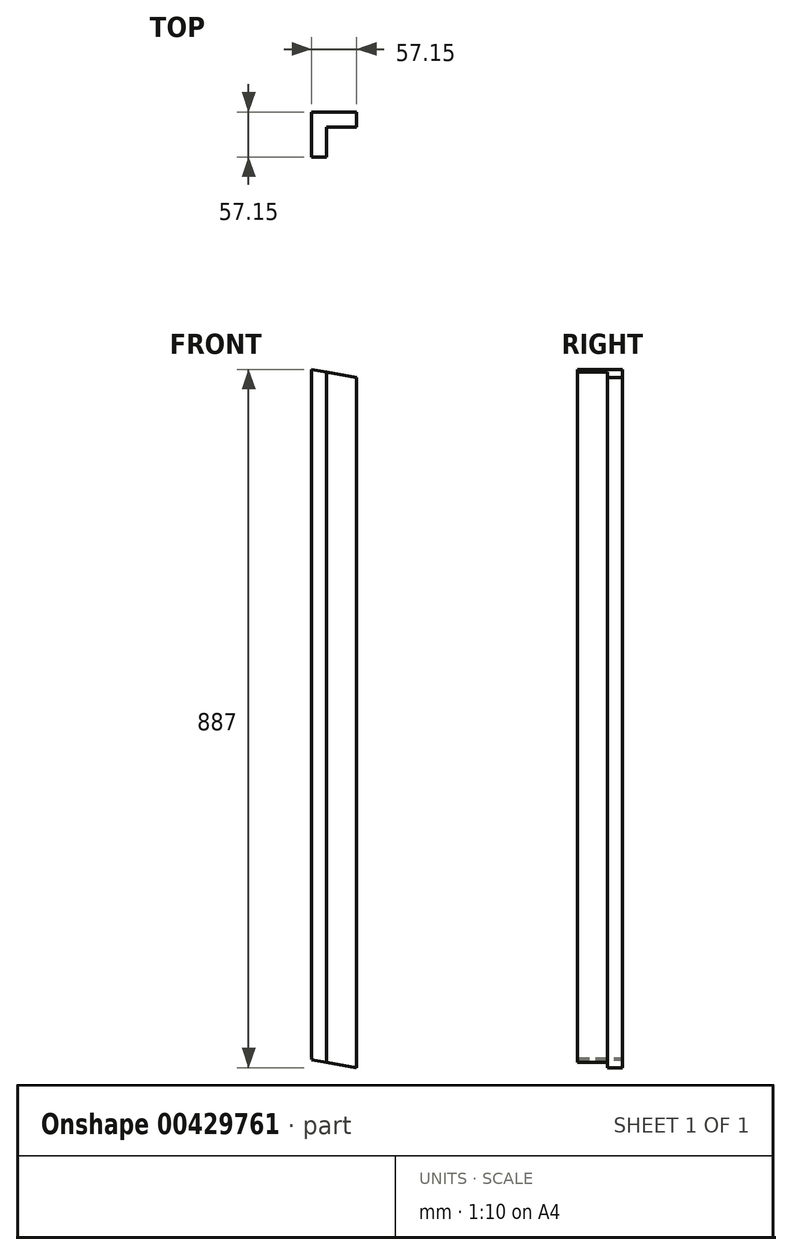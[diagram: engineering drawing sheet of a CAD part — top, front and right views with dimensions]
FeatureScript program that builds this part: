
annotation { "Feature Type Name" : "Feature", "Feature Type Description" : "" }
export const myFeature = defineFeature(function(context is Context, id is Id, definition is map)
    precondition{}
    {
        {
            var Q0;
            Q0=qCreatedBy(makeId("Top.planeOp"),FACE);
            var sketch = newSketch(context, id + "F0", { "sketchPlane" : qUnion([Q0])});
            skLineSegment(sketch, "E0", {"start": v(0, 0) * mm, "end": v(57.15, 0) * mm});
            skLineSegment(sketch, "E1", {"start": v(57.15, 0) * mm, "end": v(57.15, -19.05) * mm});
            skLineSegment(sketch, "E2", {"start": v(57.15, -19.05) * mm, "end": v(19.05, -19.05) * mm});
            skLineSegment(sketch, "E3", {"start": v(19.05, -19.05) * mm, "end": v(19.05, -57.15) * mm});
            skLineSegment(sketch, "E4", {"start": v(19.05, -57.15) * mm, "end": v(0, -57.15) * mm});
            skLineSegment(sketch, "E5", {"start": v(0, -57.15) * mm, "end": v(0, 0) * mm});
            skSolve(sketch);
        }
        {
            var Q0;
            Q0=qSketchRegion(id+"F0",true);
            extrude(context, id + "F1", {"entities" : qUnion([Q0]), "depth" : 1016 * mm});
        }
        {
            var Q0;
            Q0=makeQuery(id+"F1.opExtrude","SWEPT_FACE",FACE,{"disambiguationData":[OSD([sQuery(id+"F0.wireOp",EDGE,"E0")])]});
            var sketch = newSketch(context, id + "F2", { "sketchPlane" : qUnion([Q0])});
            skLineSegment(sketch, "E6", {"start": v(-57.15, 0) * mm, "end": v(0, 10.08) * mm});
            skLineSegment(sketch, "E7", {"start": v(0, 10.08) * mm, "end": v(0, 0) * mm});
            skLineSegment(sketch, "E8", {"start": v(0, 0) * mm, "end": v(-57.15, 0) * mm});
            skLineSegment(sketch, "E9", {"start": v(0, 1016) * mm, "end": v(-57.15, 1016) * mm});
            skLineSegment(sketch, "E10", {"start": v(-57.15, 1016) * mm, "end": v(-57.15, 876.92) * mm});
            skLineSegment(sketch, "E11", {"start": v(-57.15, 876.92) * mm, "end": v(0, 887) * mm});
            skLineSegment(sketch, "E12", {"start": v(0, 887) * mm, "end": v(0, 1016) * mm});
            skSolve(sketch);
        }
        {
            var Q0;
            Q0 = qSketchRegion(id + "F2", true);
            extrude(context, id + "F3", {"entities" : qUnion([Q0]), "operationType" : NewBodyOperationType.REMOVE, "endBound" : BoundingType.THROUGH_ALL, "oppositeDirection" : true, "depth" : 25.4 * mm});
        }
        {
            var Q0;
            Q0=makeQuery(id+"F1.opExtrude","SWEPT_FACE",FACE,{"disambiguationData":[OSD([sQuery(id+"F0.wireOp",EDGE,"E0")])]});
            var sketch = newSketch(context, id + "F4", { "sketchPlane" : qUnion([Q0])});
            skLineSegment(sketch, "E13", {"start": v(0, 10.08) * mm, "end": v(-0.44, 12.58) * mm});
            skLineSegment(sketch, "E14", {"start": v(-0.44, 12.58) * mm, "end": v(0, 12.66) * mm});
            skLineSegment(sketch, "E15", {"start": v(0, 12.66) * mm, "end": v(0, 10.08) * mm});
            skSolve(sketch);
        }
        {
            var Q0;
            Q0 = qSketchRegion(id + "F4", true);
            extrude(context, id + "F5", {"entities" : qUnion([Q0]), "operationType" : NewBodyOperationType.REMOVE, "endBound" : BoundingType.THROUGH_ALL, "oppositeDirection" : true, "depth" : 25.4 * mm});
        }
    });
